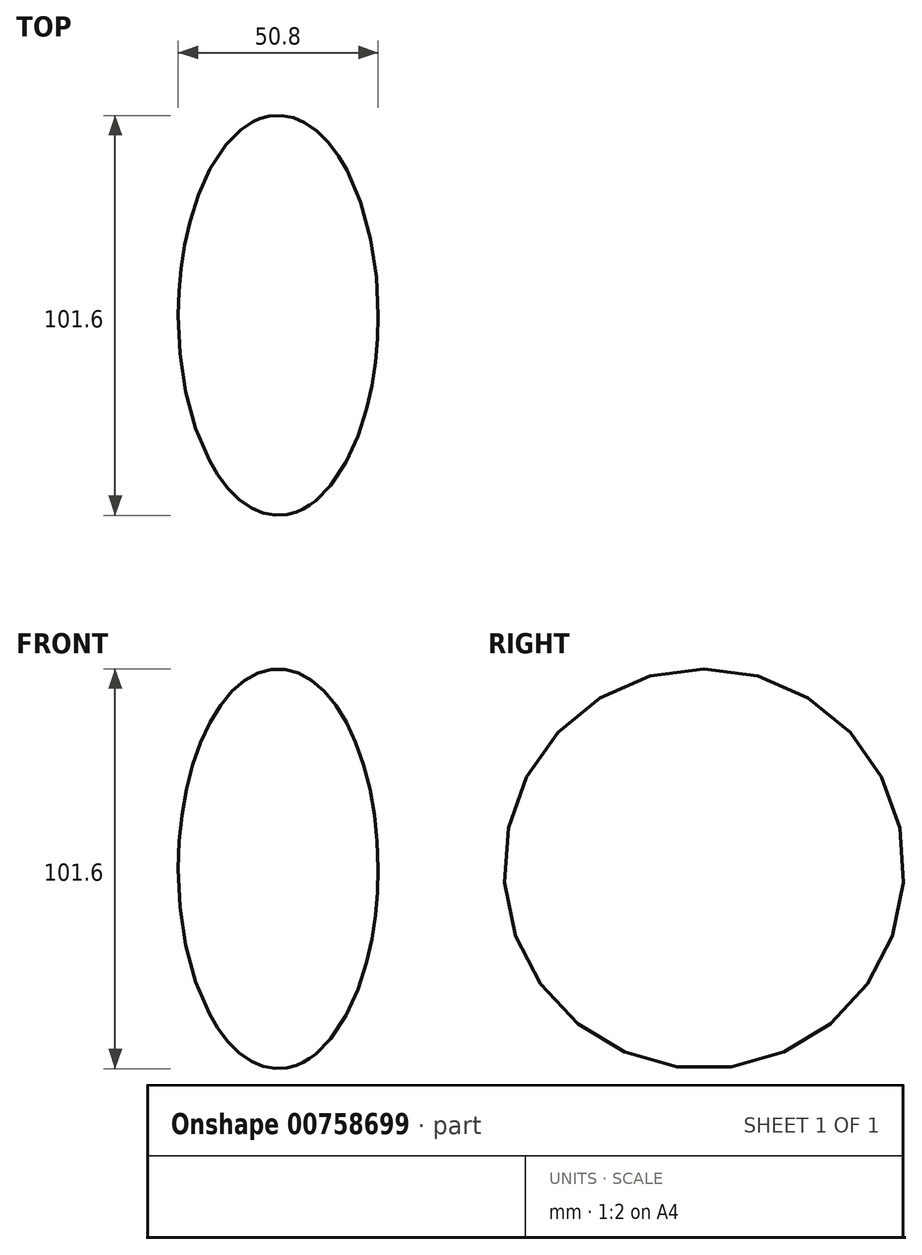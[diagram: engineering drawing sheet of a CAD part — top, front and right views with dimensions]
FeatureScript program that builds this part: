
annotation { "Feature Type Name" : "Feature", "Feature Type Description" : "" }
export const myFeature = defineFeature(function(context is Context, id is Id, definition is map)
    precondition{}
    {
        {
            var Q0;
            Q0=qCreatedBy(makeId("Front.planeOp"),FACE);
            var sketch = newSketch(context, id + "F0", { "sketchPlane" : qUnion([Q0])});
            skLineSegment(sketch, "E0", {"start": v(-70.15, 0) * mm, "end": v(55.58, 0) * mm});
            skSolve(sketch);
        }
        {
            var Q0;
            Q0=qCreatedBy(makeId("Front.planeOp"),FACE);
            var sketch = newSketch(context, id + "F1", { "sketchPlane" : qUnion([Q0])});
            skEllipse(sketch, "E1", {"center": v(0, 0) * mm, "majorRadius": 50.8 * mm, "minorRadius": 25.4 * mm, "majorAxis": v(0, 1)});
            skLineSegment(sketch, "E2", {"start": v(25.4, 0) * mm, "end": v(-25.4, 0) * mm});
            skSolve(sketch);
        }
        {
            var Q0;
            {var subQ0=sQuery(id+"F1.wireOp",EDGE,"E2");Q0=makeQuery(id+"F1.imprint","IMPRINT",FACE,{"disambiguationData":[TD([[makeQuery(id+"F1.imprint","IMPRINT",EDGE,{"derivedFrom":subQ0}),-1.0]])]});}
            var Q1;
            Q1=sQuery(id+"F0.wireOp",EDGE,"E0");
            revolve(context, id + "F2", {"surfaceOperationType" : NewSurfaceOperationType.NEW, "entities" : qUnion([Q0]), "axis" : qUnion([Q1]), "revolveType" : RevolveType.FULL});
        }
    });
